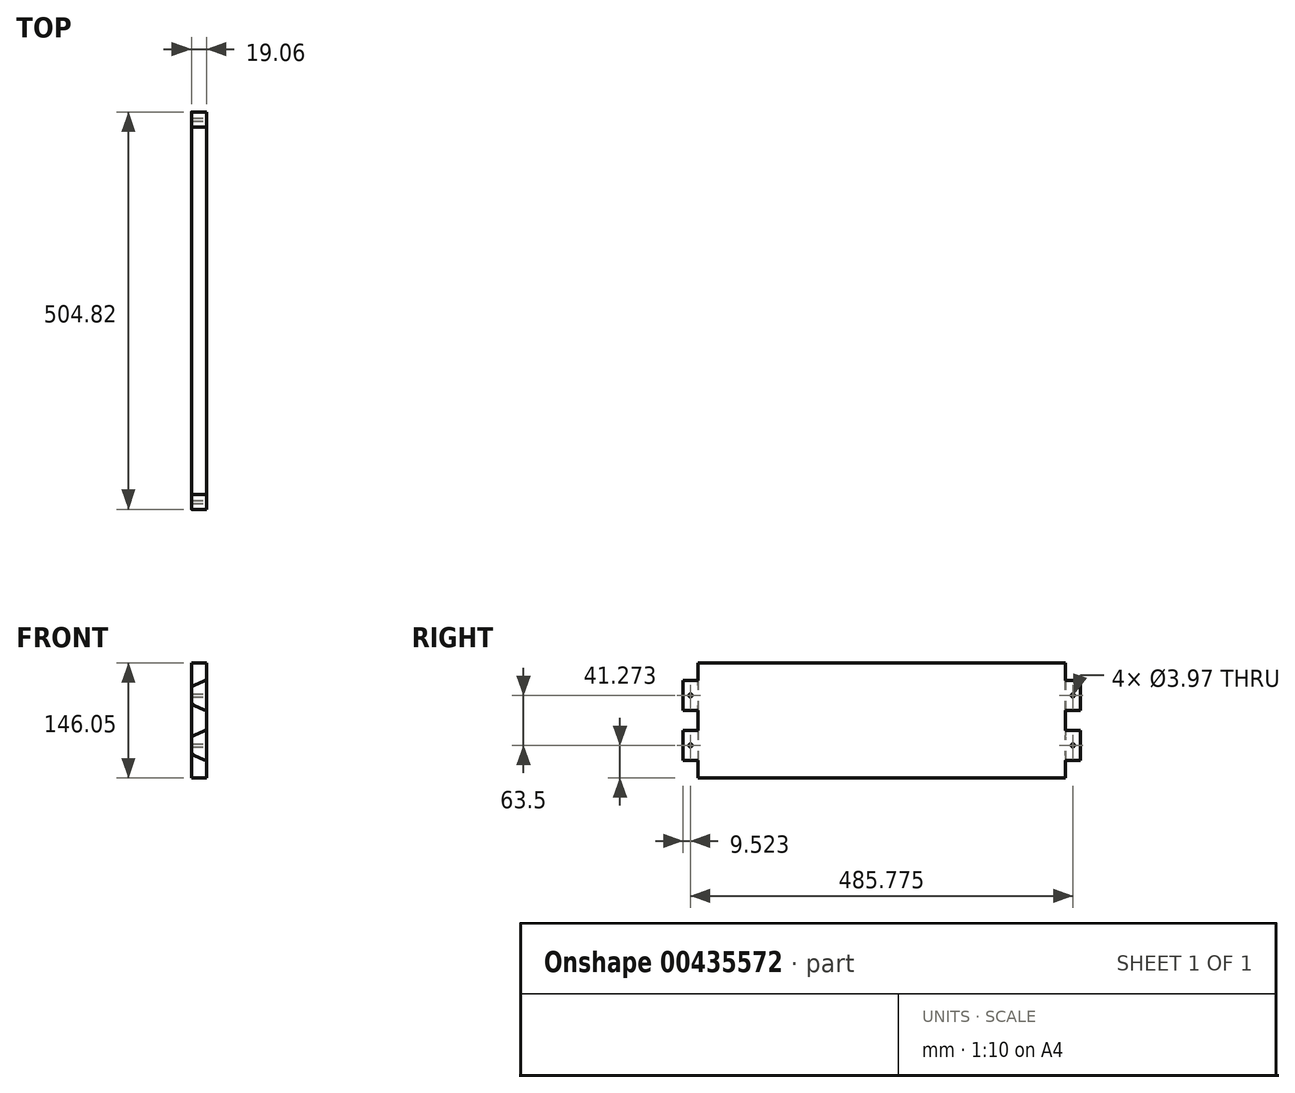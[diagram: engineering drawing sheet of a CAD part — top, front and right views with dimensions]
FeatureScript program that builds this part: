
annotation { "Feature Type Name" : "Feature", "Feature Type Description" : "" }
export const myFeature = defineFeature(function(context is Context, id is Id, definition is map)
    precondition{}
    {
        {
            var Q0;
            Q0=qCreatedBy(makeId("Front.planeOp"),FACE);
            var sketch = newSketch(context, id + "F0", { "sketchPlane" : qUnion([Q0])});
            skLineSegment(sketch, "E0.bottom", {"start": v(-9.53, 71.44) * mm, "end": v(9.52, 71.44) * mm});
            skLineSegment(sketch, "E0.top", {"start": v(-9.53, -74.61) * mm, "end": v(9.52, -74.61) * mm});
            skLineSegment(sketch, "E0.left", {"start": v(-9.52, 71.44) * mm, "end": v(-9.53, -74.61) * mm});
            skLineSegment(sketch, "E0.right", {"start": v(9.53, 71.44) * mm, "end": v(9.52, -74.61) * mm});
            skLineSegment(sketch, "E1.MirrorCS", {"start": v(-9.31, 49.21) * mm, "end": v(-9.53, 49.21) * mm});
            skLineSegment(sketch, "E2.MirrorCS", {"start": v(-9.52, 11.11) * mm, "end": v(-9.31, 11.11) * mm});
            skLineSegment(sketch, "E3.MirrorCS", {"start": v(-9.31, -52.39) * mm, "end": v(-9.53, -52.39) * mm});
            skArc(sketch, "E4.MirrorCS", {"start": v(-9.31, -14.29) * mm, "mid": v(-7.97, -14.43) * mm, "end": v(-6.69, -14.86) * mm});
            skArc(sketch, "E5.MirrorCS", {"start": v(-6.69, 48.64) * mm, "mid": v(-7.97, 49.07) * mm, "end": v(-9.31, 49.21) * mm});
            skArc(sketch, "E6.MirrorCS", {"start": v(-9.31, 11.11) * mm, "mid": v(-7.97, 11.26) * mm, "end": v(-6.69, 11.68) * mm});
            skArc(sketch, "E7.MirrorCS", {"start": v(-6.69, -51.82) * mm, "mid": v(-7.97, -52.24) * mm, "end": v(-9.31, -52.39) * mm});
            skLineSegment(sketch, "E8.MirrorCS", {"start": v(-9.53, -14.29) * mm, "end": v(-9.31, -14.29) * mm});
            skArc(sketch, "E9.MirrorCS", {"start": v(5.8, -20.53) * mm, "mid": v(8.51, -22.88) * mm, "end": v(9.52, -26.31) * mm});
            skLineSegment(sketch, "E10.MirrorCS", {"start": v(-6.69, 11.68) * mm, "end": v(5.8, 17.36) * mm});
            skArc(sketch, "E11.MirrorCS", {"start": v(5.8, 17.36) * mm, "mid": v(8.51, 19.7) * mm, "end": v(9.52, 23.14) * mm});
            skArc(sketch, "E12.MirrorCS", {"start": v(9.52, -40.36) * mm, "mid": v(8.51, -43.8) * mm, "end": v(5.8, -46.14) * mm});
            skArc(sketch, "E13.MirrorCS", {"start": v(9.52, 37.19) * mm, "mid": v(8.51, 40.62) * mm, "end": v(5.8, 42.97) * mm});
            skLineSegment(sketch, "E14.MirrorCS", {"start": v(-6.69, -14.86) * mm, "end": v(5.8, -20.53) * mm});
            skLineSegment(sketch, "E15.MirrorCS", {"start": v(5.8, 42.97) * mm, "end": v(-6.69, 48.64) * mm});
            skLineSegment(sketch, "E16.MirrorCS", {"start": v(5.8, -46.14) * mm, "end": v(-6.69, -51.82) * mm});
            skPoint(sketch, "E17.MirrorP", {"position": v(9.52, 19.05) * mm});
            skPoint(sketch, "E18.MirrorP", {"position": v(9.52, -22.22) * mm});
            skPoint(sketch, "E19.MirrorP", {"position": v(-7.94, 49.21) * mm});
            skPoint(sketch, "E20.MirrorP", {"position": v(9.52, 41.27) * mm});
            skPoint(sketch, "E21.MirrorP", {"position": v(-7.94, -52.39) * mm});
            skPoint(sketch, "E22.MirrorP", {"position": v(9.52, -44.45) * mm});
            skPoint(sketch, "E23.MirrorP", {"position": v(-7.94, -14.29) * mm});
            skPoint(sketch, "E24.MirrorP", {"position": v(-7.94, 11.11) * mm});
            skSolve(sketch);
        }
        {
            var Q0;
            {var subQ2=sQuery(id+"F0.wireOp",EDGE,"E0.top");Q0=makeQuery(id+"F0.imprint","IMPRINT",FACE,{"disambiguationData":[TD([[makeQuery(id+"F0.imprint","IMPRINT",EDGE,{"derivedFrom":subQ2}),1.0]])]});}
            var Q1;
            {var subQ0=sQuery(id+"F0.wireOp",EDGE,"E3.MirrorCS");Q1=makeQuery(id+"F0.imprint","IMPRINT",FACE,{"disambiguationData":[TD([[makeQuery(id+"F0.imprint","IMPRINT",EDGE,{"derivedFrom":subQ0}),-1.0]])]});}
            var Q2;
            {var subQ0=sQuery(id+"F0.wireOp",EDGE,"E2.MirrorCS");Q2=makeQuery(id+"F0.imprint","IMPRINT",FACE,{"disambiguationData":[TD([[makeQuery(id+"F0.imprint","IMPRINT",EDGE,{"derivedFrom":subQ0}),-1.0]])]});}
            var Q3;
            {var subQ0=sQuery(id+"F0.wireOp",EDGE,"E1.MirrorCS");Q3=makeQuery(id+"F0.imprint","IMPRINT",FACE,{"disambiguationData":[TD([[makeQuery(id+"F0.imprint","IMPRINT",EDGE,{"derivedFrom":subQ0}),1.0]])]});}
            var Q4;
            {var subQ2=sQuery(id+"F0.wireOp",EDGE,"E0.bottom");Q4=makeQuery(id+"F0.imprint","IMPRINT",FACE,{"disambiguationData":[TD([[makeQuery(id+"F0.imprint","IMPRINT",EDGE,{"derivedFrom":subQ2}),-1.0]])]});}
            extrude(context, id + "F1", {"entities" : qUnion([Q0, Q1, Q2, Q3, Q4]), "depth" : 252.4 * mm, "offsetDistance" : 25.4 * mm});
        }
        {
            var Q0;
            {var subQ2=sQuery(id+"F0.wireOp",EDGE,"E0.top");Q0=makeQuery(id+"F0.imprint","IMPRINT",FACE,{"disambiguationData":[TD([[makeQuery(id+"F0.imprint","IMPRINT",EDGE,{"derivedFrom":subQ2}),1.0]])]});}
            var Q1;
            {var subQ0=sQuery(id+"F0.wireOp",EDGE,"E3.MirrorCS");Q1=makeQuery(id+"F0.imprint","IMPRINT",FACE,{"disambiguationData":[TD([[makeQuery(id+"F0.imprint","IMPRINT",EDGE,{"derivedFrom":subQ0}),-1.0]])]});}
            var Q2;
            {var subQ0=sQuery(id+"F0.wireOp",EDGE,"E2.MirrorCS");Q2=makeQuery(id+"F0.imprint","IMPRINT",FACE,{"disambiguationData":[TD([[makeQuery(id+"F0.imprint","IMPRINT",EDGE,{"derivedFrom":subQ0}),-1.0]])]});}
            var Q3;
            {var subQ0=sQuery(id+"F0.wireOp",EDGE,"E1.MirrorCS");Q3=makeQuery(id+"F0.imprint","IMPRINT",FACE,{"disambiguationData":[TD([[makeQuery(id+"F0.imprint","IMPRINT",EDGE,{"derivedFrom":subQ0}),1.0]])]});}
            var Q4;
            {var subQ2=sQuery(id+"F0.wireOp",EDGE,"E0.bottom");Q4=makeQuery(id+"F0.imprint","IMPRINT",FACE,{"disambiguationData":[TD([[makeQuery(id+"F0.imprint","IMPRINT",EDGE,{"derivedFrom":subQ2}),-1.0]])]});}
            extrude(context, id + "F2", {"entities" : qUnion([Q0, Q1, Q2, Q3, Q4]), "operationType" : NewBodyOperationType.ADD, "oppositeDirection" : true, "depth" : 252.4 * mm, "offsetDistance" : 25.4 * mm});
        }
        {
            var Q0;
            Q0=makeQuery(id+"F1.opExtrude","CAP_FACE",FACE,{"disambiguationData":[OSD([sQuery(id+"F0.wireOp",EDGE,"E0.bottom"),sQuery(id+"F0.wireOp",EDGE,"E0.top"),sQuery(id+"F0.wireOp",EDGE,"E0.left"),sQuery(id+"F0.wireOp",EDGE,"E0.right")])],"isStart":false});
            var sketch = newSketch(context, id + "F3", { "sketchPlane" : qUnion([Q0])});
            skLineSegment(sketch, "E25.MirrorCS", {"start": v(9.31, -52.39) * mm, "end": v(9.53, -52.39) * mm});
            skLineSegment(sketch, "E26.MirrorCS", {"start": v(9.52, -14.29) * mm, "end": v(9.31, -14.29) * mm});
            skLineSegment(sketch, "E27.MirrorCS", {"start": v(9.31, 49.21) * mm, "end": v(9.53, 49.21) * mm});
            skArc(sketch, "E28.MirrorCS", {"start": v(9.31, 11.11) * mm, "mid": v(7.97, 11.26) * mm, "end": v(6.69, 11.68) * mm});
            skArc(sketch, "E29.MirrorCS", {"start": v(6.69, -51.82) * mm, "mid": v(7.97, -52.24) * mm, "end": v(9.31, -52.39) * mm});
            skArc(sketch, "E30.MirrorCS", {"start": v(9.31, -14.29) * mm, "mid": v(7.97, -14.43) * mm, "end": v(6.69, -14.86) * mm});
            skArc(sketch, "E31.MirrorCS", {"start": v(6.69, 48.64) * mm, "mid": v(7.97, 49.07) * mm, "end": v(9.31, 49.21) * mm});
            skLineSegment(sketch, "E32.MirrorCS", {"start": v(9.53, 11.11) * mm, "end": v(9.31, 11.11) * mm});
            skArc(sketch, "E33.MirrorCS", {"start": v(-5.8, 17.36) * mm, "mid": v(-8.51, 19.7) * mm, "end": v(-9.52, 23.14) * mm});
            skLineSegment(sketch, "E34.MirrorCS", {"start": v(6.69, -14.86) * mm, "end": v(-5.8, -20.53) * mm});
            skArc(sketch, "E35.MirrorCS", {"start": v(-5.8, -20.53) * mm, "mid": v(-8.51, -22.88) * mm, "end": v(-9.52, -26.31) * mm});
            skArc(sketch, "E36.MirrorCS", {"start": v(-9.52, 37.19) * mm, "mid": v(-8.51, 40.62) * mm, "end": v(-5.8, 42.97) * mm});
            skArc(sketch, "E37.MirrorCS", {"start": v(-9.52, -40.36) * mm, "mid": v(-8.51, -43.8) * mm, "end": v(-5.8, -46.14) * mm});
            skLineSegment(sketch, "E38.MirrorCS", {"start": v(6.69, 11.68) * mm, "end": v(-5.8, 17.36) * mm});
            skLineSegment(sketch, "E39.MirrorCS", {"start": v(-5.8, -46.14) * mm, "end": v(6.69, -51.82) * mm});
            skLineSegment(sketch, "E40.MirrorCS", {"start": v(-5.8, 42.97) * mm, "end": v(6.69, 48.64) * mm});
            skPoint(sketch, "E41.MirrorP", {"position": v(-9.52, -19.05) * mm});
            skPoint(sketch, "E42.MirrorP", {"position": v(-9.52, 22.22) * mm});
            skPoint(sketch, "E43.MirrorP", {"position": v(7.94, -49.21) * mm});
            skPoint(sketch, "E44.MirrorP", {"position": v(-9.52, -41.27) * mm});
            skPoint(sketch, "E45.MirrorP", {"position": v(7.94, 52.39) * mm});
            skPoint(sketch, "E46.MirrorP", {"position": v(-9.52, 44.45) * mm});
            skPoint(sketch, "E47.MirrorP", {"position": v(7.94, 14.29) * mm});
            skPoint(sketch, "E48.MirrorP", {"position": v(7.94, -11.11) * mm});
            skSolve(sketch);
        }
        {
            var Q0;
            Q0=makeQuery(id+"F2.opExtrude","CAP_FACE",FACE,{"disambiguationData":[OSD([sQuery(id+"F0.wireOp",EDGE,"E0.bottom"),sQuery(id+"F0.wireOp",EDGE,"E0.top"),sQuery(id+"F0.wireOp",EDGE,"E0.left"),sQuery(id+"F0.wireOp",EDGE,"E0.right")])],"isStart":false});
            var sketch = newSketch(context, id + "F4", { "sketchPlane" : qUnion([Q0])});
            skLineSegment(sketch, "E49.MirrorCS", {"start": v(-9.31, 49.21) * mm, "end": v(-9.53, 49.21) * mm});
            skLineSegment(sketch, "E50.MirrorCS", {"start": v(-9.52, 11.11) * mm, "end": v(-9.31, 11.11) * mm});
            skLineSegment(sketch, "E51.MirrorCS", {"start": v(-9.31, -52.39) * mm, "end": v(-9.52, -52.39) * mm});
            skArc(sketch, "E52.MirrorCS", {"start": v(-9.31, -14.29) * mm, "mid": v(-7.97, -14.43) * mm, "end": v(-6.69, -14.86) * mm});
            skArc(sketch, "E53.MirrorCS", {"start": v(-6.69, 48.64) * mm, "mid": v(-7.97, 49.07) * mm, "end": v(-9.31, 49.21) * mm});
            skArc(sketch, "E54.MirrorCS", {"start": v(-9.31, 11.11) * mm, "mid": v(-7.97, 11.26) * mm, "end": v(-6.69, 11.68) * mm});
            skArc(sketch, "E55.MirrorCS", {"start": v(-6.69, -51.82) * mm, "mid": v(-7.97, -52.24) * mm, "end": v(-9.31, -52.39) * mm});
            skLineSegment(sketch, "E56.MirrorCS", {"start": v(-9.52, -14.29) * mm, "end": v(-9.31, -14.29) * mm});
            skArc(sketch, "E57.MirrorCS", {"start": v(5.8, -20.53) * mm, "mid": v(8.51, -22.88) * mm, "end": v(9.52, -26.31) * mm});
            skLineSegment(sketch, "E58.MirrorCS", {"start": v(-6.69, 11.68) * mm, "end": v(5.8, 17.36) * mm});
            skArc(sketch, "E59.MirrorCS", {"start": v(5.8, 17.36) * mm, "mid": v(8.51, 19.7) * mm, "end": v(9.52, 23.14) * mm});
            skArc(sketch, "E60.MirrorCS", {"start": v(9.52, -40.36) * mm, "mid": v(8.51, -43.8) * mm, "end": v(5.8, -46.14) * mm});
            skArc(sketch, "E61.MirrorCS", {"start": v(9.52, 37.19) * mm, "mid": v(8.51, 40.62) * mm, "end": v(5.8, 42.97) * mm});
            skLineSegment(sketch, "E62.MirrorCS", {"start": v(-6.69, -14.86) * mm, "end": v(5.8, -20.53) * mm});
            skLineSegment(sketch, "E63.MirrorCS", {"start": v(5.8, 42.97) * mm, "end": v(-6.69, 48.64) * mm});
            skLineSegment(sketch, "E64.MirrorCS", {"start": v(5.8, -46.14) * mm, "end": v(-6.69, -51.82) * mm});
            skPoint(sketch, "E65.MirrorP", {"position": v(9.52, 19.05) * mm});
            skPoint(sketch, "E66.MirrorP", {"position": v(9.52, -22.22) * mm});
            skPoint(sketch, "E67.MirrorP", {"position": v(-7.94, 49.21) * mm});
            skPoint(sketch, "E68.MirrorP", {"position": v(9.52, 41.27) * mm});
            skPoint(sketch, "E69.MirrorP", {"position": v(-7.94, -52.39) * mm});
            skPoint(sketch, "E70.MirrorP", {"position": v(9.52, -44.45) * mm});
            skPoint(sketch, "E71.MirrorP", {"position": v(-7.94, -14.29) * mm});
            skPoint(sketch, "E72.MirrorP", {"position": v(-7.94, 11.11) * mm});
            skSolve(sketch);
        }
        {
            var Q0;
            {var subQ3=sQuery(id+"F4.wireOp",EDGE,"E49.MirrorCS");Q0=makeQuery(id+"F4.imprint","IMPRINT",FACE,{"disambiguationData":[TD([[makeQuery(id+"F4.imprint","IMPRINT",EDGE,{"derivedFrom":subQ3}),-1.0]])]});}
            var Q1;
            {var subQ1=sQuery(id+"F4.wireOp",EDGE,"E50.MirrorCS");Q1=makeQuery(id+"F4.imprint","IMPRINT",FACE,{"disambiguationData":[TD([[makeQuery(id+"F4.imprint","IMPRINT",EDGE,{"derivedFrom":subQ1}),-1.0]])]});}
            var Q2;
            {var subQ2=sQuery(id+"F4.wireOp",EDGE,"E51.MirrorCS");Q2=makeQuery(id+"F4.imprint","IMPRINT",FACE,{"disambiguationData":[TD([[makeQuery(id+"F4.imprint","IMPRINT",EDGE,{"derivedFrom":subQ2}),1.0]])]});}
            extrude(context, id + "F5", {"entities" : qUnion([Q0, Q1, Q2]), "operationType" : NewBodyOperationType.REMOVE, "oppositeDirection" : true, "depth" : 19.05 * mm, "offsetDistance" : 25.4 * mm});
        }
        {
            var Q0;
            {var subQ2=sQuery(id+"F3.wireOp",EDGE,"E27.MirrorCS");Q0=makeQuery(id+"F3.imprint","IMPRINT",FACE,{"disambiguationData":[TD([[makeQuery(id+"F3.imprint","IMPRINT",EDGE,{"derivedFrom":subQ2}),1.0]])]});}
            var Q1;
            {var subQ4=sQuery(id+"F3.wireOp",EDGE,"E26.MirrorCS");Q1=makeQuery(id+"F3.imprint","IMPRINT",FACE,{"disambiguationData":[TD([[makeQuery(id+"F3.imprint","IMPRINT",EDGE,{"derivedFrom":subQ4}),-1.0]])]});}
            var Q2;
            {var subQ3=sQuery(id+"F3.wireOp",EDGE,"E25.MirrorCS");Q2=makeQuery(id+"F3.imprint","IMPRINT",FACE,{"disambiguationData":[TD([[makeQuery(id+"F3.imprint","IMPRINT",EDGE,{"derivedFrom":subQ3}),-1.0]])]});}
            extrude(context, id + "F6", {"entities" : qUnion([Q0, Q1, Q2]), "operationType" : NewBodyOperationType.REMOVE, "oppositeDirection" : true, "depth" : 19.05 * mm, "offsetDistance" : 25.4 * mm});
        }
        {
            var Q0;
            {var subQ0=sQuery(id+"F0.wireOp",EDGE,"E0.right");Q0=makeQuery(id+"F2.boolean.opBoolean","MERGE",FACE,{"derivedFrom":[makeQuery(id+"F1.opExtrude","SWEPT_FACE",FACE,{"disambiguationData":[OSD([subQ0])]}),makeQuery(id+"F2.opExtrude","SWEPT_FACE",FACE,{"disambiguationData":[OSD([subQ0])]})]});}
            var sketch = newSketch(context, id + "F7", { "sketchPlane" : qUnion([Q0])});
            skCircle(sketch, "E73", {"center": v(-242.89, 30.16) * mm, "radius": 1.98 * mm});
            skPoint(sketch, "E73.centerSnap0", {"position": v(-252.41, 30.16) * mm});
            skPoint(sketch, "E73.centerSnap1", {"position": v(-242.89, 49.21) * mm});
            skPoint(sketch, "E74.centerSnap0", {"position": v(-252.41, -33.34) * mm});
            skPoint(sketch, "E74.centerSnap1", {"position": v(-242.89, -14.29) * mm});
            skCircle(sketch, "E75", {"center": v(-242.89, -33.34) * mm, "radius": 1.98 * mm});
            skCircle(sketch, "E76", {"center": v(242.89, -33.34) * mm, "radius": 1.98 * mm});
            skPoint(sketch, "E77", {"position": v(252.41, -33.34) * mm});
            skPoint(sketch, "E78", {"position": v(242.89, -14.29) * mm});
            skCircle(sketch, "E79", {"center": v(242.89, 30.16) * mm, "radius": 1.98 * mm});
            skPoint(sketch, "E80", {"position": v(252.41, 30.16) * mm});
            skPoint(sketch, "E81", {"position": v(242.89, 49.21) * mm});
            skSolve(sketch);
        }
        {
            var Q0;
            Q0=makeQuery(id+"F7.imprint","IMPRINT",FACE,{"disambiguationData":[TD([[makeQuery(id+"F7.imprint","IMPRINT",EDGE,{"derivedFrom":sQuery(id+"F7.wireOp",EDGE,"E75")}),1.0]])]});
            var Q1;
            Q1=makeQuery(id+"F7.imprint","IMPRINT",FACE,{"disambiguationData":[TD([[makeQuery(id+"F7.imprint","IMPRINT",EDGE,{"derivedFrom":sQuery(id+"F7.wireOp",EDGE,"E73")}),1.0]])]});
            var Q2;
            Q2=makeQuery(id+"F7.imprint","IMPRINT",FACE,{"disambiguationData":[TD([[makeQuery(id+"F7.imprint","IMPRINT",EDGE,{"derivedFrom":sQuery(id+"F7.wireOp",EDGE,"E76")}),1.0]])]});
            var Q3;
            Q3=makeQuery(id+"F7.imprint","IMPRINT",FACE,{"disambiguationData":[TD([[makeQuery(id+"F7.imprint","IMPRINT",EDGE,{"derivedFrom":sQuery(id+"F7.wireOp",EDGE,"E79")}),1.0]])]});
            extrude(context, id + "F8", {"entities" : qUnion([Q0, Q1, Q2, Q3]), "operationType" : NewBodyOperationType.REMOVE, "oppositeDirection" : true, "depth" : 19.05 * mm, "offsetDistance" : 25.4 * mm});
        }
    });
